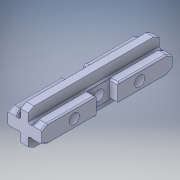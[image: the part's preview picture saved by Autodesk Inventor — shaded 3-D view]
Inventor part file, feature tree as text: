
AUTODESK INVENTOR PART (.ipt)
format: ipt  version: 2016 (Build 200138000, 138)  size: 348,672 bytes
history: native  units: in
note: dims shown in document units (in); Inventor stores cm internally (conversion verified against a paired STEP export)
features: fillet x1
ambient origin geometry x8: Origin, YZ Plane, XZ Plane, XY Plane, X Axis, Y Axis, Z Axis, Center Point
bodies: Solid1 (feature_tree)
feature tree (1):
  fillet  "Fillet2"  [1 undecoded]
note: 1 required parameter value undecoded (feature->parameter linkage not recoverable at this tier; creation-order binding heuristic only, values carry confidence <= 0.55)
